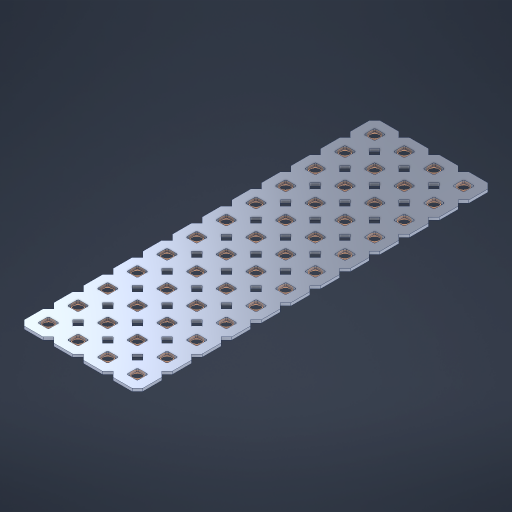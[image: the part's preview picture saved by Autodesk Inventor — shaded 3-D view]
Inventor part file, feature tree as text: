
AUTODESK INVENTOR PART (.ipt)
format: ipt  version: 2023 (Build 270158000, 158)  size: 817,664 bytes
history: native  units: in
note: dims shown in document units (in); Inventor stores cm internally (conversion verified against a paired STEP export)
features: other x49, extrude x47, sketch x2, pattern_linear x1
ambient origin geometry x8: Origin, YZ Plane, XZ Plane, XY Plane, X Axis, Y Axis, Z Axis, Center Point
bodies: Solid1 (feature_tree), Body (feature_tree)
feature tree (99):
  pattern_linear  "Rectangular Pattern1"  Spacing1=0.09in  [1 undecoded]
  sketch  "Sketch1"  dims[d1=0.5in]
  sketch  "Sketch2"  dims[d2=0.182in d3=0.09in d4=0.09in d5=0.09in d6=0.09in d7=0.09in d8=0.09in d9=0.09in d10=0.09in d11=0.02in d13=0.0in d14=0.172in d15=0.0625in d16=0.0in d19=0.5in d22=0.5in]
  other  "Srf1"
  other  "Srf126"
  other  "Srf127"
  other  "Srf128"
  other  "Srf129"
  other  "Srf130"
  other  "Srf131"
  other  "Srf250"
  other  "Srf251"
  other  "Srf252"
  other  "Srf253"
  other  "Srf254"
  other  "Srf268"
  other  "Srf269"
  other  "Srf270"
  other  "Srf271"
  other  "Srf272"
  other  "Srf273"
  other  "Srf274"
  other  "Srf275"
  other  "Srf276"
  other  "Srf277"
  other  "Srf278"
  other  "Srf279"
  other  "Srf293"
  other  "Srf294"
  other  "Srf295"
  other  "Srf296"
  other  "Srf297"
  other  "Srf298"
  other  "Srf299"
  other  "Srf300"
  other  "Srf301"
  other  "Srf302"
  other  "Srf303"
  other  "Srf304"
  other  "Srf318"
  other  "Srf319"
  other  "Srf320"
  other  "Srf321"
  other  "Srf322"
  other  "Srf323"
  other  "Srf324"
  other  "Srf325"
  other  "Srf326"
  other  "Srf327"
  other  "Srf328"
  other  "Srf329"
  other  "Circle"
  extrude  "ExtrusionSrf126"  Depth=0.09in
  extrude  "ExtrusionSrf127"  Depth=0.09in
  extrude  "ExtrusionSrf128"  Depth=0.09in
  extrude  "ExtrusionSrf129"  Depth=0.09in
  extrude  "ExtrusionSrf130"  Depth=0.09in
  extrude  "ExtrusionSrf131"  Depth=0.09in
  extrude  "ExtrusionSrf250"  Depth=0.09in
  extrude  "ExtrusionSrf251"  Depth=0.02in
  extrude  "ExtrusionSrf252"  TaperAngle=0.0deg  [1 undecoded]
  extrude  "ExtrusionSrf253"  Depth=0.5in
  extrude  "ExtrusionSrf254"  Depth=0.5in TaperAngle=0.0deg
  extrude  "ExtrusionSrf268"  Depth=0.5in
  extrude  "ExtrusionSrf269"  Depth=0.5in
  extrude  "ExtrusionSrf270"  [1 undecoded]
  extrude  "ExtrusionSrf271"  [1 undecoded]
  extrude  "ExtrusionSrf272"  [1 undecoded]
  extrude  "ExtrusionSrf273"  [1 undecoded]
  extrude  "ExtrusionSrf274"  [1 undecoded]
  extrude  "ExtrusionSrf275"  [1 undecoded]
  extrude  "ExtrusionSrf276"  [1 undecoded]
  extrude  "ExtrusionSrf277"  [1 undecoded]
  extrude  "ExtrusionSrf278"  [1 undecoded]
  extrude  "ExtrusionSrf279"  [1 undecoded]
  extrude  "ExtrusionSrf293"  [1 undecoded]
  extrude  "ExtrusionSrf294"  [1 undecoded]
  extrude  "ExtrusionSrf295"  [1 undecoded]
  extrude  "ExtrusionSrf296"  [1 undecoded]
  extrude  "ExtrusionSrf297"  [1 undecoded]
  extrude  "ExtrusionSrf298"  [1 undecoded]
  extrude  "ExtrusionSrf299"  [1 undecoded]
  extrude  "ExtrusionSrf300"  [1 undecoded]
  extrude  "ExtrusionSrf301"  [1 undecoded]
  extrude  "ExtrusionSrf302"  [1 undecoded]
  extrude  "ExtrusionSrf303"  [1 undecoded]
  extrude  "ExtrusionSrf304"  [1 undecoded]
  extrude  "ExtrusionSrf318"  [1 undecoded]
  extrude  "ExtrusionSrf319"  [1 undecoded]
  extrude  "ExtrusionSrf320"  [1 undecoded]
  extrude  "ExtrusionSrf321"  [1 undecoded]
  extrude  "ExtrusionSrf322"  [1 undecoded]
  extrude  "ExtrusionSrf323"  [1 undecoded]
  extrude  "ExtrusionSrf324"  [1 undecoded]
  extrude  "ExtrusionSrf325"  [1 undecoded]
  extrude  "ExtrusionSrf326"  [1 undecoded]
  extrude  "ExtrusionSrf327"  [1 undecoded]
  extrude  "ExtrusionSrf328"  [1 undecoded]
  extrude  "ExtrusionSrf329"  [1 undecoded]
note: 36 required parameter values undecoded (feature->parameter linkage not recoverable at this tier; creation-order binding heuristic only, values carry confidence <= 0.55)
